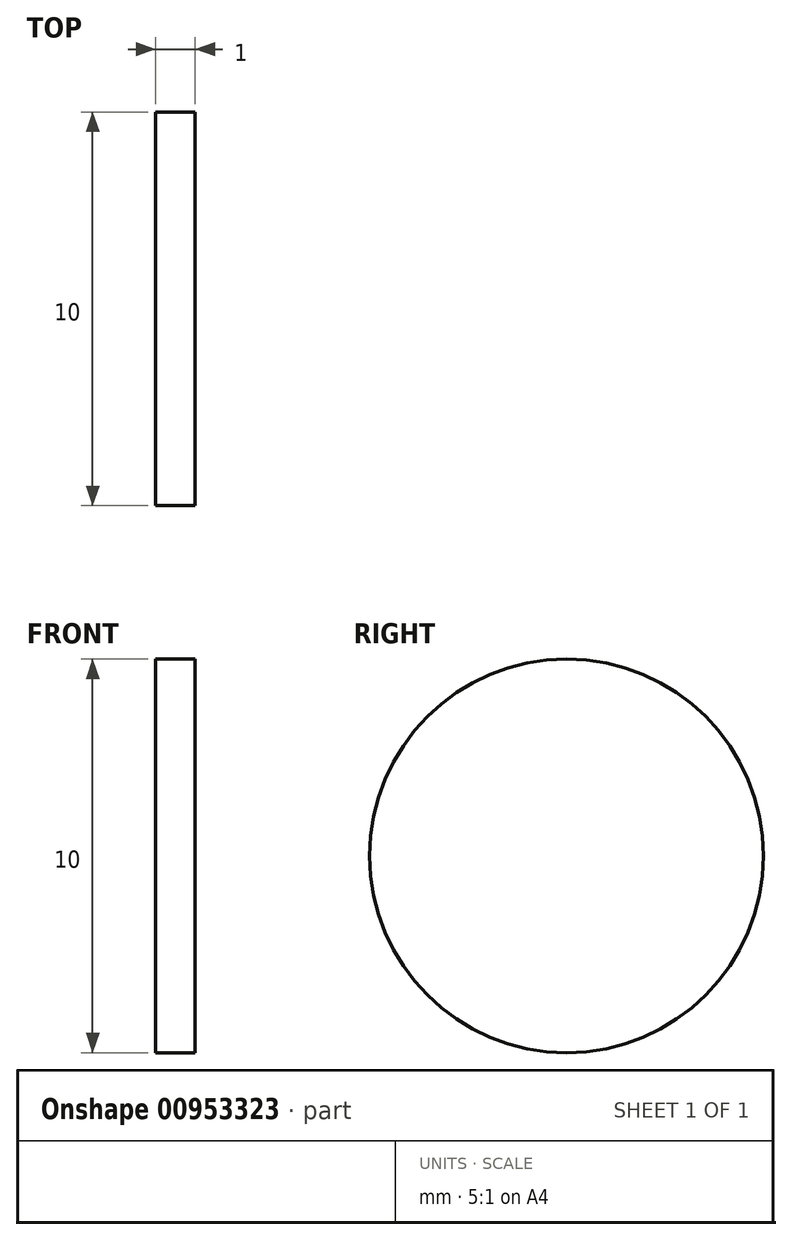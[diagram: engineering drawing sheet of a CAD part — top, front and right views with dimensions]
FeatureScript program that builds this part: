
annotation { "Feature Type Name" : "Feature", "Feature Type Description" : "" }
export const myFeature = defineFeature(function(context is Context, id is Id, definition is map)
    precondition{}
    {
        {
            var Q0;
            Q0=qCreatedBy(makeId("Right.planeOp"),FACE);
            var sketch = newSketch(context, id + "F0", { "sketchPlane" : qUnion([Q0])});
            skCircle(sketch, "E0", {"center": v(0, 0) * mm, "radius": 5 * mm});
            skSolve(sketch);
        }
        {
            var Q0;
            Q0 = qSketchRegion(id + "F0", true);
            extrude(context, id + "F1", {"entities" : qUnion([Q0]), "depth" : 1 * mm, "offsetDistance" : 25.4 * mm});
        }
    });
